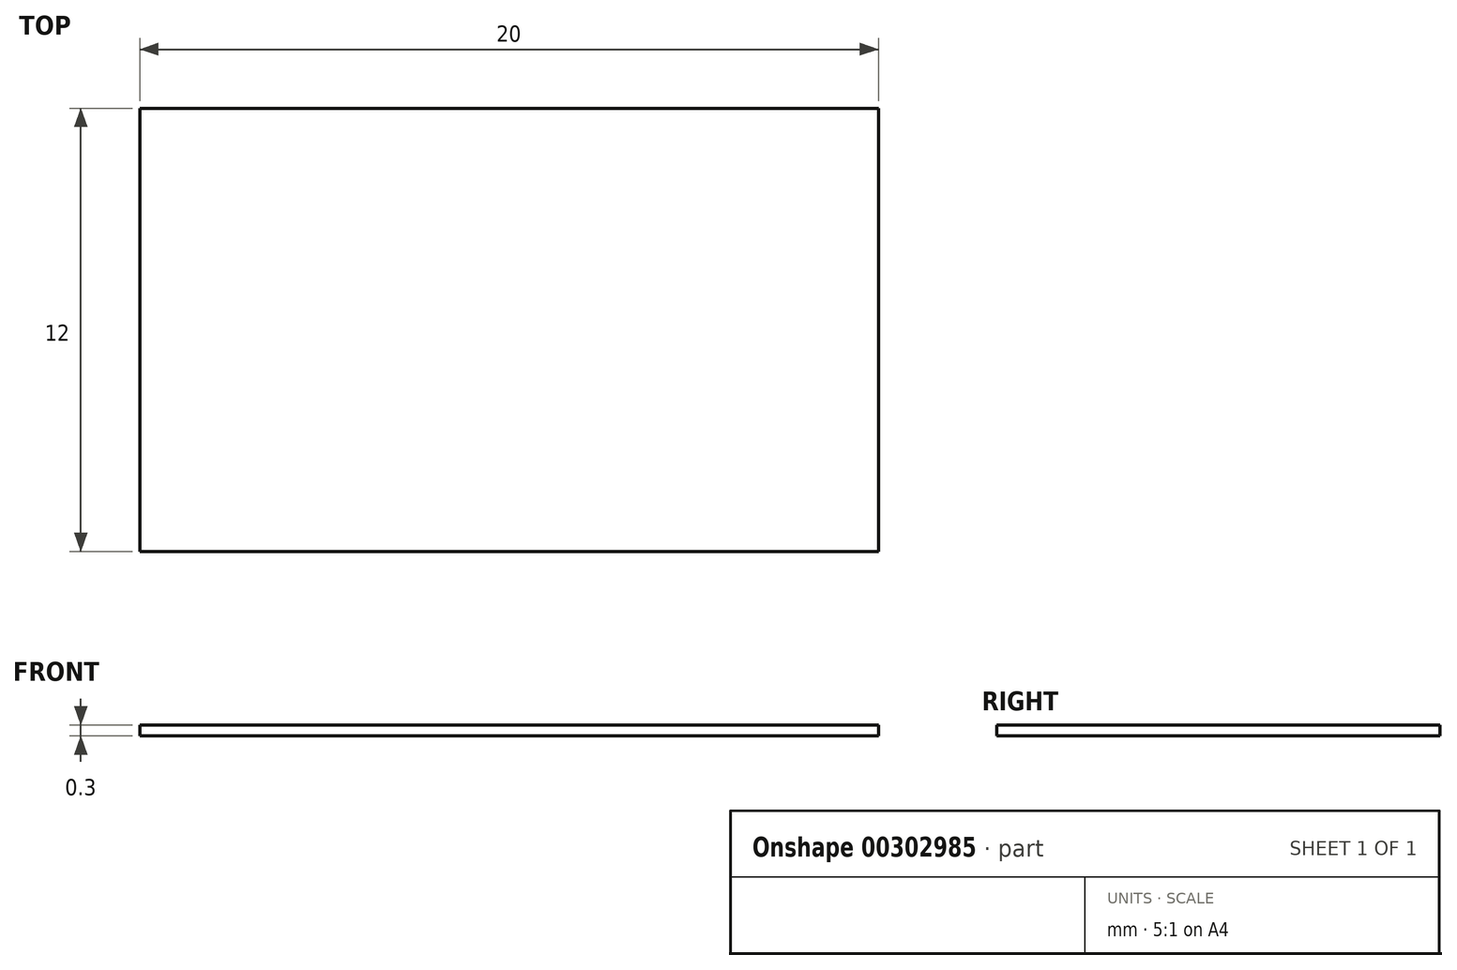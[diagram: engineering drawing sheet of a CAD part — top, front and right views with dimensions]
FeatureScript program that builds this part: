
annotation { "Feature Type Name" : "Feature", "Feature Type Description" : "" }
export const myFeature = defineFeature(function(context is Context, id is Id, definition is map)
    precondition{}
    {
        {
            var Q0;
            Q0=qCreatedBy(makeId("Top.planeOp"),FACE);
            var sketch = newSketch(context, id + "F0", { "sketchPlane" : qUnion([Q0])});
            skLineSegment(sketch, "E0.bottom", {"start": v(10, 6) * mm, "end": v(-10, 6) * mm});
            skLineSegment(sketch, "E0.top", {"start": v(10, -6) * mm, "end": v(-10, -6) * mm});
            skLineSegment(sketch, "E0.left", {"start": v(10, 6) * mm, "end": v(10, -6) * mm});
            skLineSegment(sketch, "E0.right", {"start": v(-10, 6) * mm, "end": v(-10, -6) * mm});
            skPoint(sketch, "E0.middle", {"position": v(0, 0) * mm});
            skSolve(sketch);
        }
        {
            var Q0;
            Q0=makeQuery(id+"F0.imprint","IMPRINT",FACE,{"disambiguationData":[TD([[makeQuery(id+"F0.imprint","IMPRINT",EDGE,{"derivedFrom":sQuery(id+"F0.wireOp",EDGE,"E0.bottom")}),1.0]])]});
            extrude(context, id + "F1", {"entities" : qUnion([Q0]), "depth" : 0.3 * mm, "offsetDistance" : 25 * mm});
        }
    });
